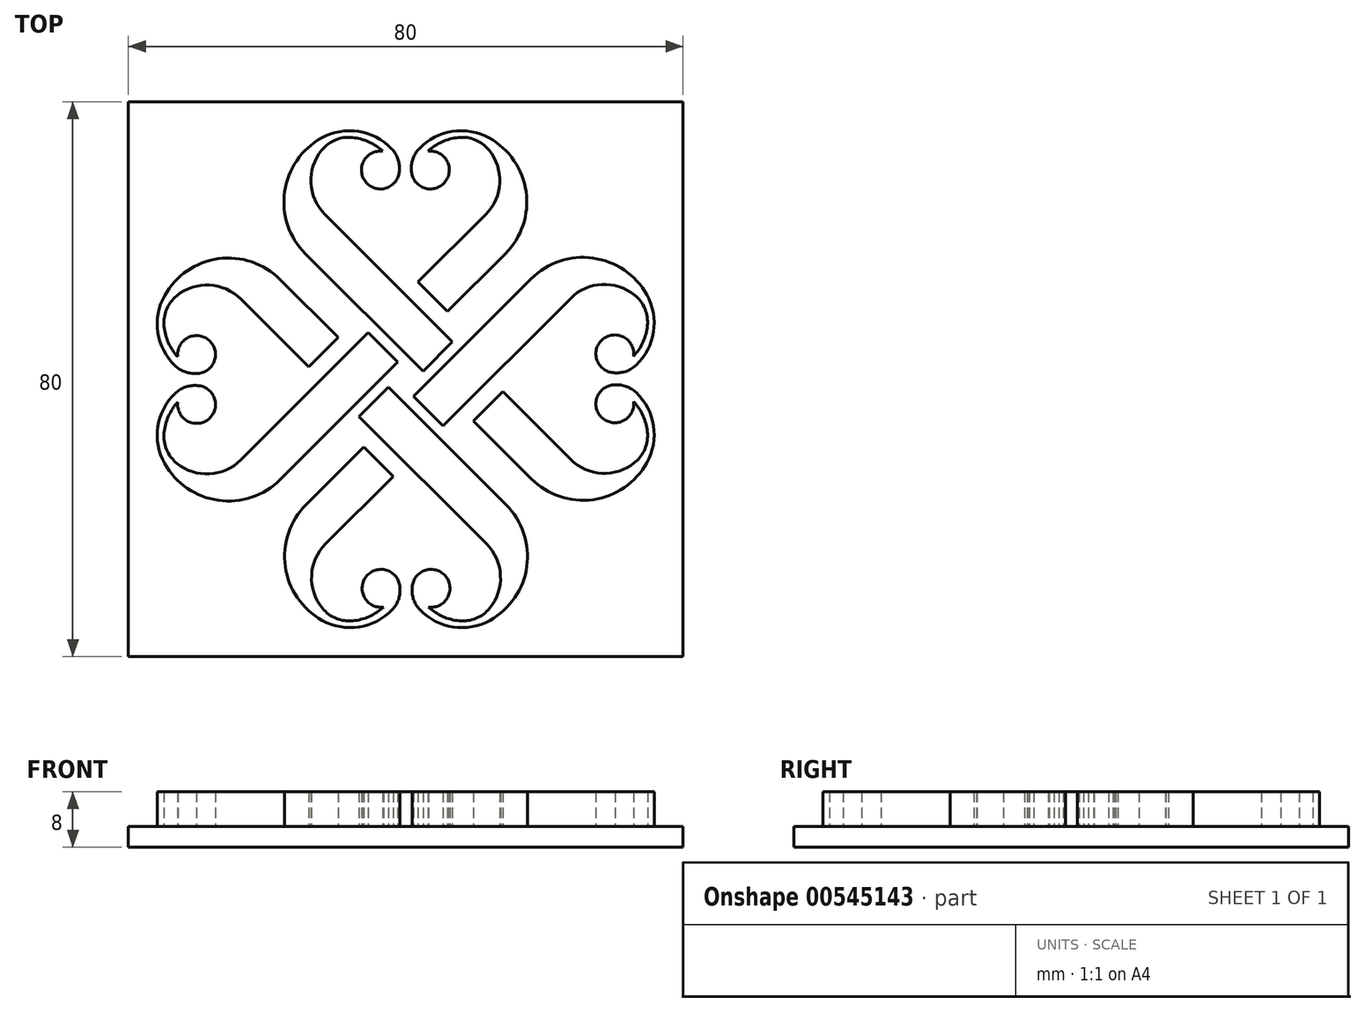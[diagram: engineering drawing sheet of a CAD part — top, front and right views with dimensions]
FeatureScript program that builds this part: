
annotation { "Feature Type Name" : "Feature", "Feature Type Description" : "" }
export const myFeature = defineFeature(function(context is Context, id is Id, definition is map)
    precondition{}
    {
        {
            var Q0;
            Q0=qCreatedBy(makeId("Top.planeOp"),FACE);
            var sketch = newSketch(context, id + "F0", { "sketchPlane" : qUnion([Q0])});
            skLineSegment(sketch, "E0", {"start": v(2.5, 1.14) * mm, "end": v(6.73, 5.39) * mm});
            skLineSegment(sketch, "E1", {"start": v(2.5, 1.14) * mm, "end": v(-14.48, 18.11) * mm});
            skLineSegment(sketch, "E2", {"start": v(6.73, 5.39) * mm, "end": v(-11.65, 23.77) * mm});
            skArc(sketch, "E3", {"start": v(-11.65, 23.77) * mm, "mid": v(-13.67, 28.31) * mm, "end": v(-12.12, 33.03) * mm});
            skArc(sketch, "E4", {"start": v(-12.12, 33.03) * mm, "mid": v(-10.15, 34.5) * mm, "end": v(-7.72, 34.86) * mm});
            skArc(sketch, "E5", {"start": v(-7.72, 34.86) * mm, "mid": v(-5.35, 34.23) * mm, "end": v(-3.3, 32.88) * mm});
            skArc(sketch, "E6", {"start": v(-14.48, 18.11) * mm, "mid": v(-17.47, 27.02) * mm, "end": v(-12.16, 34.78) * mm});
            skArc(sketch, "E7", {"start": v(-12.16, 34.78) * mm, "mid": v(-6.83, 35.74) * mm, "end": v(-2.02, 33.24) * mm});
            skArc(sketch, "E8", {"start": v(-3.3, 32.88) * mm, "mid": v(-5.69, 28.35) * mm, "end": v(-0.92, 30.2) * mm});
            skArc(sketch, "E9", {"start": v(-2.02, 33.24) * mm, "mid": v(-1.15, 31.84) * mm, "end": v(-0.92, 30.2) * mm});
            skLineSegment(sketch, "E10", {"start": v(1.14, -2.5) * mm, "end": v(5.39, -6.73) * mm});
            skLineSegment(sketch, "E11", {"start": v(1.14, -2.5) * mm, "end": v(18.11, 14.48) * mm});
            skLineSegment(sketch, "E12", {"start": v(5.39, -6.73) * mm, "end": v(23.77, 11.65) * mm});
            skArc(sketch, "E13", {"start": v(23.77, 11.65) * mm, "mid": v(28.31, 13.67) * mm, "end": v(33.03, 12.12) * mm});
            skArc(sketch, "E14", {"start": v(33.03, 12.12) * mm, "mid": v(34.5, 10.15) * mm, "end": v(34.86, 7.72) * mm});
            skArc(sketch, "E15", {"start": v(34.86, 7.72) * mm, "mid": v(34.23, 5.35) * mm, "end": v(32.88, 3.3) * mm});
            skArc(sketch, "E16", {"start": v(18.11, 14.48) * mm, "mid": v(27.02, 17.47) * mm, "end": v(34.78, 12.16) * mm});
            skArc(sketch, "E17", {"start": v(34.78, 12.16) * mm, "mid": v(35.74, 6.83) * mm, "end": v(33.24, 2.02) * mm});
            skArc(sketch, "E18", {"start": v(32.88, 3.3) * mm, "mid": v(28.35, 5.69) * mm, "end": v(30.2, 0.92) * mm});
            skArc(sketch, "E19", {"start": v(33.24, 2.02) * mm, "mid": v(31.84, 1.15) * mm, "end": v(30.2, 0.92) * mm});
            skLineSegment(sketch, "E20", {"start": v(-2.5, -1.14) * mm, "end": v(-6.73, -5.39) * mm});
            skLineSegment(sketch, "E21", {"start": v(-2.5, -1.14) * mm, "end": v(14.48, -18.11) * mm});
            skLineSegment(sketch, "E22", {"start": v(-6.73, -5.39) * mm, "end": v(11.65, -23.77) * mm});
            skArc(sketch, "E23", {"start": v(11.65, -23.77) * mm, "mid": v(13.67, -28.31) * mm, "end": v(12.12, -33.03) * mm});
            skArc(sketch, "E24", {"start": v(12.12, -33.03) * mm, "mid": v(10.15, -34.5) * mm, "end": v(7.72, -34.86) * mm});
            skArc(sketch, "E25", {"start": v(7.72, -34.86) * mm, "mid": v(5.35, -34.23) * mm, "end": v(3.3, -32.88) * mm});
            skArc(sketch, "E26", {"start": v(14.48, -18.11) * mm, "mid": v(17.47, -27.02) * mm, "end": v(12.16, -34.78) * mm});
            skArc(sketch, "E27", {"start": v(12.16, -34.78) * mm, "mid": v(6.83, -35.74) * mm, "end": v(2.02, -33.24) * mm});
            skArc(sketch, "E28", {"start": v(3.3, -32.88) * mm, "mid": v(5.69, -28.35) * mm, "end": v(0.92, -30.2) * mm});
            skArc(sketch, "E29", {"start": v(2.02, -33.24) * mm, "mid": v(1.15, -31.84) * mm, "end": v(0.92, -30.2) * mm});
            skLineSegment(sketch, "E30", {"start": v(-1.14, 2.5) * mm, "end": v(-5.39, 6.73) * mm});
            skLineSegment(sketch, "E31", {"start": v(-1.14, 2.5) * mm, "end": v(-18.11, -14.48) * mm});
            skLineSegment(sketch, "E32", {"start": v(-5.39, 6.73) * mm, "end": v(-23.77, -11.65) * mm});
            skArc(sketch, "E33", {"start": v(-23.77, -11.65) * mm, "mid": v(-28.31, -13.67) * mm, "end": v(-33.03, -12.12) * mm});
            skArc(sketch, "E34", {"start": v(-33.03, -12.12) * mm, "mid": v(-34.5, -10.15) * mm, "end": v(-34.86, -7.72) * mm});
            skArc(sketch, "E35", {"start": v(-34.86, -7.72) * mm, "mid": v(-34.23, -5.35) * mm, "end": v(-32.88, -3.3) * mm});
            skArc(sketch, "E36", {"start": v(-18.11, -14.48) * mm, "mid": v(-27.02, -17.47) * mm, "end": v(-34.78, -12.16) * mm});
            skArc(sketch, "E37", {"start": v(-34.78, -12.16) * mm, "mid": v(-35.74, -6.83) * mm, "end": v(-33.24, -2.02) * mm});
            skArc(sketch, "E38", {"start": v(-32.88, -3.3) * mm, "mid": v(-28.35, -5.69) * mm, "end": v(-30.2, -0.92) * mm});
            skArc(sketch, "E39", {"start": v(-33.24, -2.02) * mm, "mid": v(-31.84, -1.15) * mm, "end": v(-30.2, -0.92) * mm});
            skArc(sketch, "E40.MirrorCS", {"start": v(11.55, 23.77) * mm, "mid": v(13.57, 28.31) * mm, "end": v(12.02, 33.03) * mm});
            skArc(sketch, "E41.MirrorCS", {"start": v(1.93, 33.24) * mm, "mid": v(1.06, 31.84) * mm, "end": v(0.82, 30.2) * mm});
            skArc(sketch, "E42.MirrorCS", {"start": v(3.2, 32.88) * mm, "mid": v(5.6, 28.35) * mm, "end": v(0.82, 30.2) * mm});
            skArc(sketch, "E43.MirrorCS", {"start": v(7.62, 34.86) * mm, "mid": v(5.25, 34.23) * mm, "end": v(3.2, 32.88) * mm});
            skArc(sketch, "E44.MirrorCS", {"start": v(12.02, 33.03) * mm, "mid": v(10.05, 34.5) * mm, "end": v(7.62, 34.86) * mm});
            skArc(sketch, "E45.MirrorCS", {"start": v(12.06, 34.78) * mm, "mid": v(6.73, 35.74) * mm, "end": v(1.93, 33.24) * mm});
            skArc(sketch, "E46.MirrorCS", {"start": v(14.38, 18.11) * mm, "mid": v(17.37, 27.02) * mm, "end": v(12.06, 34.78) * mm});
            skLineSegment(sketch, "E47", {"start": v(1.8, 14) * mm, "end": v(6.03, 9.76) * mm});
            skLineSegment(sketch, "E48.trimOffspring", {"start": v(1.8, 14) * mm, "end": v(11.55, 23.77) * mm});
            skLineSegment(sketch, "E49.trimOffspring", {"start": v(6.03, 9.76) * mm, "end": v(14.38, 18.11) * mm});
            skArc(sketch, "E50.MirrorCS", {"start": v(23.77, -11.55) * mm, "mid": v(28.31, -13.57) * mm, "end": v(33.03, -12.02) * mm});
            skArc(sketch, "E51.MirrorCS", {"start": v(33.24, -1.93) * mm, "mid": v(31.84, -1.06) * mm, "end": v(30.2, -0.82) * mm});
            skArc(sketch, "E52.MirrorCS", {"start": v(32.88, -3.2) * mm, "mid": v(28.35, -5.6) * mm, "end": v(30.2, -0.82) * mm});
            skArc(sketch, "E53.MirrorCS", {"start": v(34.86, -7.62) * mm, "mid": v(34.23, -5.25) * mm, "end": v(32.88, -3.2) * mm});
            skArc(sketch, "E54.MirrorCS", {"start": v(33.03, -12.02) * mm, "mid": v(34.5, -10.05) * mm, "end": v(34.86, -7.62) * mm});
            skArc(sketch, "E55.MirrorCS", {"start": v(34.78, -12.06) * mm, "mid": v(35.74, -6.73) * mm, "end": v(33.24, -1.93) * mm});
            skArc(sketch, "E56.MirrorCS", {"start": v(18.11, -14.38) * mm, "mid": v(27.02, -17.37) * mm, "end": v(34.78, -12.06) * mm});
            skLineSegment(sketch, "E57", {"start": v(14, -1.8) * mm, "end": v(9.76, -6.03) * mm});
            skLineSegment(sketch, "E58.trimOffspring", {"start": v(14, -1.8) * mm, "end": v(23.77, -11.55) * mm});
            skLineSegment(sketch, "E59.trimOffspring", {"start": v(9.76, -6.03) * mm, "end": v(18.11, -14.38) * mm});
            skArc(sketch, "E60.MirrorCS", {"start": v(-11.55, -23.77) * mm, "mid": v(-13.57, -28.31) * mm, "end": v(-12.02, -33.03) * mm});
            skArc(sketch, "E61.MirrorCS", {"start": v(-1.93, -33.24) * mm, "mid": v(-1.06, -31.84) * mm, "end": v(-0.82, -30.2) * mm});
            skArc(sketch, "E62.MirrorCS", {"start": v(-3.2, -32.88) * mm, "mid": v(-5.6, -28.35) * mm, "end": v(-0.82, -30.2) * mm});
            skArc(sketch, "E63.MirrorCS", {"start": v(-7.62, -34.86) * mm, "mid": v(-5.25, -34.23) * mm, "end": v(-3.2, -32.88) * mm});
            skArc(sketch, "E64.MirrorCS", {"start": v(-12.02, -33.03) * mm, "mid": v(-10.05, -34.5) * mm, "end": v(-7.62, -34.86) * mm});
            skArc(sketch, "E65.MirrorCS", {"start": v(-12.06, -34.78) * mm, "mid": v(-6.73, -35.74) * mm, "end": v(-1.93, -33.24) * mm});
            skArc(sketch, "E66.MirrorCS", {"start": v(-14.38, -18.11) * mm, "mid": v(-17.37, -27.02) * mm, "end": v(-12.06, -34.78) * mm});
            skLineSegment(sketch, "E67", {"start": v(-1.8, -14) * mm, "end": v(-6.03, -9.76) * mm});
            skLineSegment(sketch, "E68.trimOffspring", {"start": v(-1.8, -14) * mm, "end": v(-11.55, -23.77) * mm});
            skLineSegment(sketch, "E69.trimOffspring", {"start": v(-6.03, -9.76) * mm, "end": v(-14.38, -18.11) * mm});
            skArc(sketch, "E70.MirrorCS", {"start": v(-23.77, 11.55) * mm, "mid": v(-28.31, 13.57) * mm, "end": v(-33.03, 12.02) * mm});
            skArc(sketch, "E71.MirrorCS", {"start": v(-33.24, 1.93) * mm, "mid": v(-31.84, 1.06) * mm, "end": v(-30.2, 0.82) * mm});
            skArc(sketch, "E72.MirrorCS", {"start": v(-32.88, 3.2) * mm, "mid": v(-28.35, 5.6) * mm, "end": v(-30.2, 0.82) * mm});
            skArc(sketch, "E73.MirrorCS", {"start": v(-34.86, 7.62) * mm, "mid": v(-34.23, 5.25) * mm, "end": v(-32.88, 3.2) * mm});
            skArc(sketch, "E74.MirrorCS", {"start": v(-33.03, 12.02) * mm, "mid": v(-34.5, 10.05) * mm, "end": v(-34.86, 7.62) * mm});
            skArc(sketch, "E75.MirrorCS", {"start": v(-34.78, 12.06) * mm, "mid": v(-35.74, 6.73) * mm, "end": v(-33.24, 1.93) * mm});
            skArc(sketch, "E76.MirrorCS", {"start": v(-18.11, 14.38) * mm, "mid": v(-27.02, 17.37) * mm, "end": v(-34.78, 12.06) * mm});
            skLineSegment(sketch, "E77", {"start": v(-14, 1.8) * mm, "end": v(-9.76, 6.03) * mm});
            skLineSegment(sketch, "E78.trimOffspring", {"start": v(-14, 1.8) * mm, "end": v(-23.77, 11.55) * mm});
            skLineSegment(sketch, "E79.trimOffspring", {"start": v(-9.76, 6.03) * mm, "end": v(-18.11, 14.38) * mm});
            skSolve(sketch);
        }
        {
            var Q0;
            Q0=makeQuery(id+"F0.imprint","IMPRINT",FACE,{"disambiguationData":[TD([[makeQuery(id+"F0.imprint","IMPRINT",EDGE,{"derivedFrom":sQuery(id+"F0.wireOp",EDGE,"E70.MirrorCS")}),-1.0]])]});
            var Q1;
            Q1=makeQuery(id+"F0.imprint","IMPRINT",FACE,{"disambiguationData":[TD([[makeQuery(id+"F0.imprint","IMPRINT",EDGE,{"derivedFrom":sQuery(id+"F0.wireOp",EDGE,"E30")}),1.0]])]});
            var Q2;
            Q2=makeQuery(id+"F0.imprint","IMPRINT",FACE,{"disambiguationData":[TD([[makeQuery(id+"F0.imprint","IMPRINT",EDGE,{"derivedFrom":sQuery(id+"F0.wireOp",EDGE,"E60.MirrorCS")}),-1.0]])]});
            var Q3;
            Q3=makeQuery(id+"F0.imprint","IMPRINT",FACE,{"disambiguationData":[TD([[makeQuery(id+"F0.imprint","IMPRINT",EDGE,{"derivedFrom":sQuery(id+"F0.wireOp",EDGE,"E20")}),1.0]])]});
            var Q4;
            Q4=makeQuery(id+"F0.imprint","IMPRINT",FACE,{"disambiguationData":[TD([[makeQuery(id+"F0.imprint","IMPRINT",EDGE,{"derivedFrom":sQuery(id+"F0.wireOp",EDGE,"E50.MirrorCS")}),-1.0]])]});
            var Q5;
            Q5=makeQuery(id+"F0.imprint","IMPRINT",FACE,{"disambiguationData":[TD([[makeQuery(id+"F0.imprint","IMPRINT",EDGE,{"derivedFrom":sQuery(id+"F0.wireOp",EDGE,"E10")}),1.0]])]});
            var Q6;
            Q6=makeQuery(id+"F0.imprint","IMPRINT",FACE,{"disambiguationData":[TD([[makeQuery(id+"F0.imprint","IMPRINT",EDGE,{"derivedFrom":sQuery(id+"F0.wireOp",EDGE,"E40.MirrorCS")}),-1.0]])]});
            var Q7;
            Q7=makeQuery(id+"F0.imprint","IMPRINT",FACE,{"disambiguationData":[TD([[makeQuery(id+"F0.imprint","IMPRINT",EDGE,{"derivedFrom":sQuery(id+"F0.wireOp",EDGE,"E0")}),1.0]])]});
            extrude(context, id + "F1", {"entities" : qUnion([Q0, Q1, Q2, Q3, Q4, Q5, Q6, Q7]), "depth" : 5 * mm, "offsetDistance" : 25 * mm});
        }
        {
            var Q0;
            Q0=qCreatedBy(makeId("Top.planeOp"),FACE);
            var sketch = newSketch(context, id + "F2", { "sketchPlane" : qUnion([Q0])});
            skLineSegment(sketch, "E80.bottom", {"start": v(-40, 40) * mm, "end": v(40, 40) * mm});
            skLineSegment(sketch, "E80.top", {"start": v(-40, -40) * mm, "end": v(40, -40) * mm});
            skLineSegment(sketch, "E80.left", {"start": v(-40, 40) * mm, "end": v(-40, -40) * mm});
            skLineSegment(sketch, "E80.right", {"start": v(40, 40) * mm, "end": v(40, -40) * mm});
            skPoint(sketch, "E80.middle", {"position": v(0, 0) * mm});
            skSolve(sketch);
        }
        {
            var Q0;
            Q0=makeQuery(id+"F2.imprint","IMPRINT",FACE,{"disambiguationData":[TD([[makeQuery(id+"F2.imprint","IMPRINT",EDGE,{"derivedFrom":sQuery(id+"F2.wireOp",EDGE,"E80.bottom")}),-1.0]])]});
            extrude(context, id + "F3", {"entities" : qUnion([Q0]), "depth" : -3 * mm, "offsetDistance" : 25 * mm});
        }
    });
